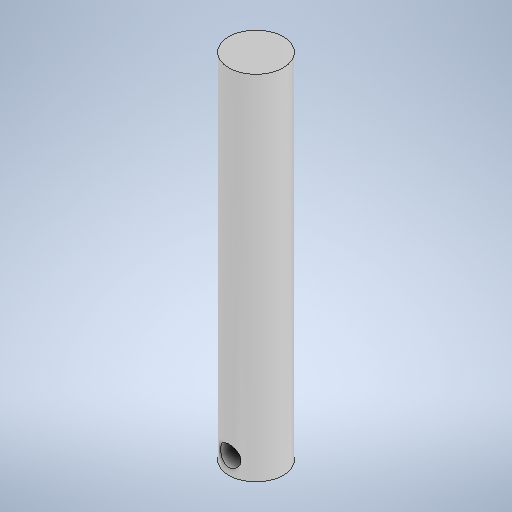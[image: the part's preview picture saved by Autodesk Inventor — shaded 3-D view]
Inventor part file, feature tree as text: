
AUTODESK INVENTOR PART (.ipt)
format: ipt  version: 2025.1 (Build 291241000, 241)  size: 248,320 bytes
history: native  units: mm
features: sketch x2, extrude x1, plane x1, hole x1
ambient origin geometry x8: Origin, YZ Plane, XZ Plane, XY Plane, X Axis, Y Axis, Z Axis, Center Point
bodies: Solid1 (feature_tree)
feature tree (5):
  extrude  "Extrusion1"  Depth=52.0mm TaperAngle=0.0deg
  plane  "Work Plane1"
  hole  "Hole1"  [1 undecoded]
  sketch  "Sketch1"  dims[d0=8.0mm d1=52.0mm d2=0.0mm]
  sketch  "Sketch2"  dims[d3=4.0mm d4=2.5mm d5=3.0mm d6=6.0mm d7=4.0mm d8=2.0mm d9=90.0deg d10=8.0mm d11=20.594885mm]
note: 1 required parameter value undecoded (feature->parameter linkage not recoverable at this tier; creation-order binding heuristic only, values carry confidence <= 0.55)
